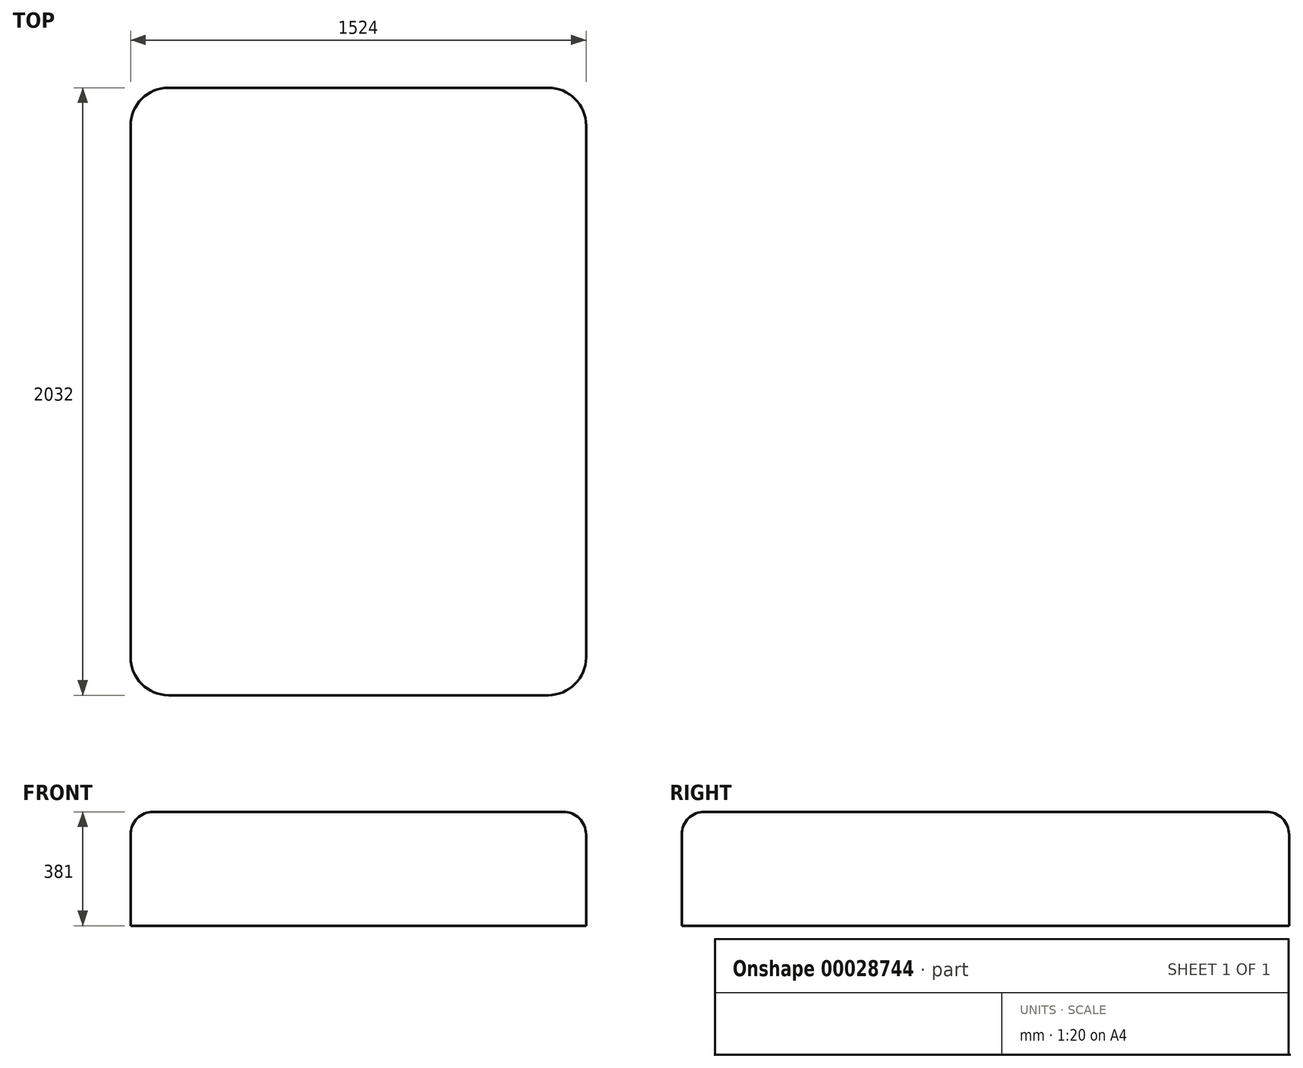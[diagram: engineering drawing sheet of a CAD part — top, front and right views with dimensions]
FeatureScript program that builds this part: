
annotation { "Feature Type Name" : "Feature", "Feature Type Description" : "" }
export const myFeature = defineFeature(function(context is Context, id is Id, definition is map)
    precondition{}
    {
        {
            var Q0;
            Q0=qCreatedBy(makeId("Top.planeOp"),FACE);
            var sketch = newSketch(context, id + "F0", { "sketchPlane" : qUnion([Q0])});
            skLineSegment(sketch, "E0.bottom", {"start": v(-1364.2, 1051.23) * mm, "end": v(-94.2, 1051.23) * mm});
            skLineSegment(sketch, "E0.top", {"start": v(-1364.2, -980.77) * mm, "end": v(-94.2, -980.77) * mm});
            skLineSegment(sketch, "E0.left", {"start": v(-1491.2, 924.23) * mm, "end": v(-1491.2, -853.77) * mm});
            skLineSegment(sketch, "E0.right", {"start": v(32.8, 924.23) * mm, "end": v(32.8, -853.77) * mm});
            skPoint(sketch, "E1.visualSharp", {"position": v(-1491.2, 1051.23) * mm});
            skArc(sketch, "E1.filletArc", {"start": v(-1364.2, 1051.23) * mm, "mid": v(-1454, 1014.03) * mm, "end": v(-1491.2, 924.23) * mm});
            skPoint(sketch, "E2.visualSharp", {"position": v(-1491.2, -980.77) * mm});
            skArc(sketch, "E2.filletArc", {"start": v(-1491.2, -853.77) * mm, "mid": v(-1454, -943.57) * mm, "end": v(-1364.2, -980.77) * mm});
            skPoint(sketch, "E3.visualSharp", {"position": v(32.8, -980.77) * mm});
            skArc(sketch, "E3.filletArc", {"start": v(-94.2, -980.77) * mm, "mid": v(-4.4, -943.57) * mm, "end": v(32.8, -853.77) * mm});
            skPoint(sketch, "E4.visualSharp", {"position": v(32.8, 1051.23) * mm});
            skArc(sketch, "E4.filletArc", {"start": v(32.8, 924.23) * mm, "mid": v(-4.4, 1014.03) * mm, "end": v(-94.2, 1051.23) * mm});
            skSolve(sketch);
        }
        {
            var Q0;
            Q0 = qSketchRegion(id + "F0", true);
            extrude(context, id + "F1", {"entities" : qUnion([Q0]), "depth" : 381 * mm});
        }
        {
            var Q0;
            Q0=makeQuery(id+"F1.opExtrude","CAP_EDGE",EDGE,{"disambiguationData":[OSD([sQuery(id+"F0.wireOp",EDGE,"E0.top")])],"isStart":false});
            var Q1;
            Q1=makeQuery(id+"F1.opExtrude","CAP_EDGE",EDGE,{"disambiguationData":[OSD([sQuery(id+"F0.wireOp",EDGE,"E0.left")])],"isStart":false});
            var Q2;
            Q2=makeQuery(id+"F1.opExtrude","CAP_EDGE",EDGE,{"disambiguationData":[OSD([sQuery(id+"F0.wireOp",EDGE,"E0.bottom")])],"isStart":false});
            var Q3;
            Q3=makeQuery(id+"F1.opExtrude","CAP_EDGE",EDGE,{"disambiguationData":[OSD([sQuery(id+"F0.wireOp",EDGE,"E0.right")])],"isStart":false});
            fillet(context, id + "F2", {"entities" : qUnion([Q0, Q1, Q2, Q3]), "radius" : 76.2 * mm, "tangentPropagation" : true, "allowEdgeOverflow" : false});
        }
    });
